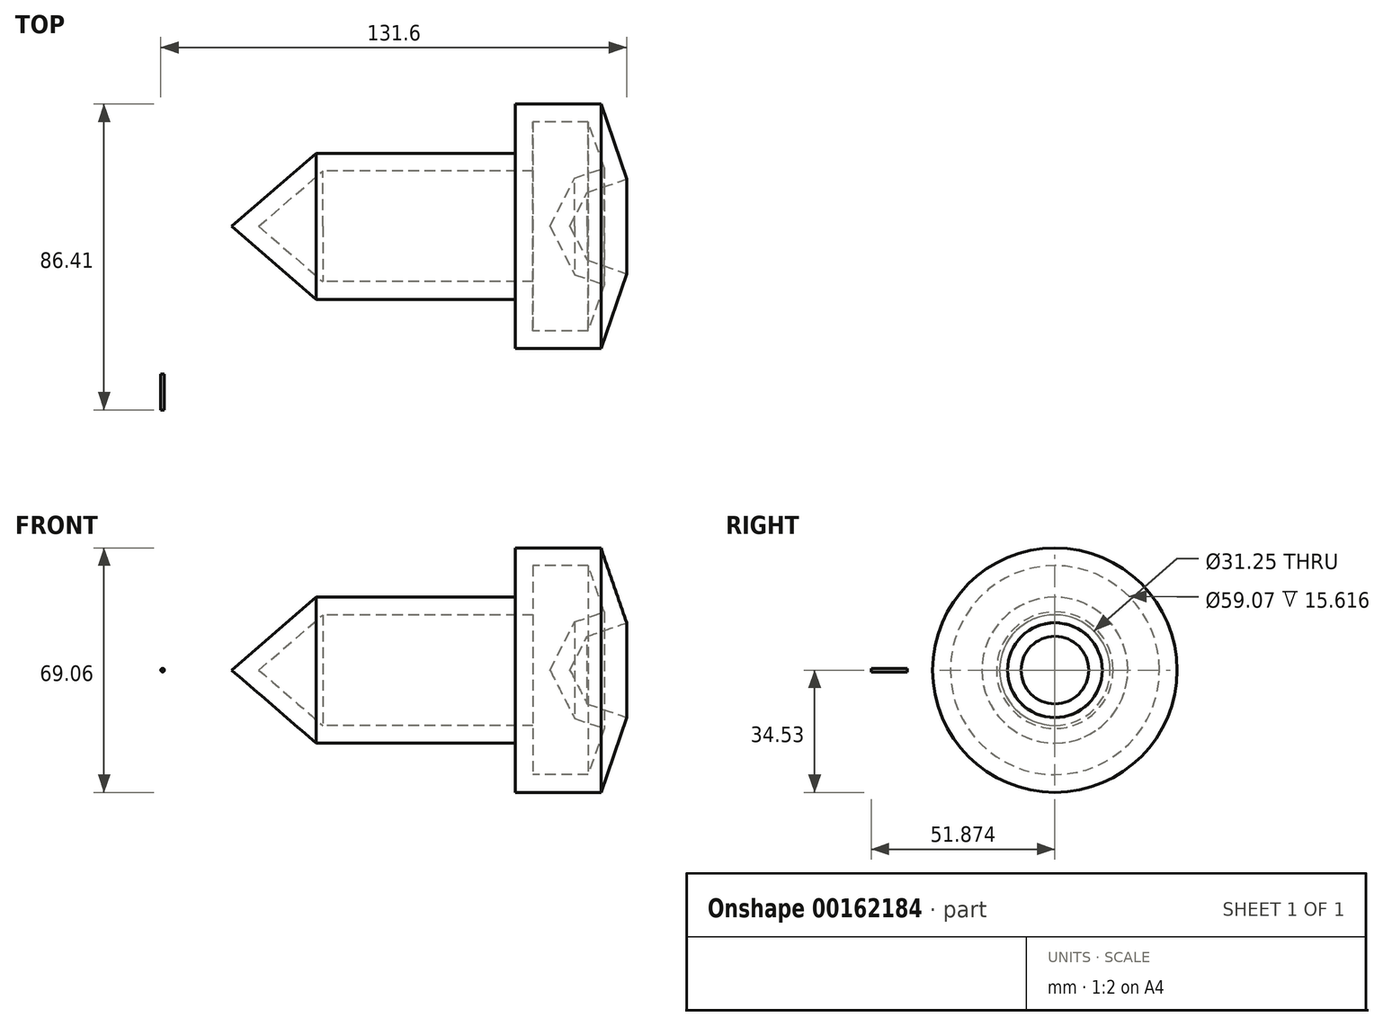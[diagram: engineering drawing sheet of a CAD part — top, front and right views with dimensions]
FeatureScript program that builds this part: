
annotation { "Feature Type Name" : "Feature", "Feature Type Description" : "" }
export const myFeature = defineFeature(function(context is Context, id is Id, definition is map)
    precondition{}
    {
        {
            var Q0;
            Q0=qCreatedBy(makeId("Top.planeOp"),FACE);
            var sketch = newSketch(context, id + "F0", { "sketchPlane" : qUnion([Q0])});
            skLineSegment(sketch, "E0", {"start": v(27.18, 41.72) * mm, "end": v(115.07, 41.72) * mm, "construction": true});
            skLineSegment(sketch, "E1", {"start": v(19.53, 41.72) * mm, "end": v(43.41, 62.35) * mm});
            skLineSegment(sketch, "E2", {"start": v(43.41, 62.35) * mm, "end": v(99.65, 62.35) * mm});
            skLineSegment(sketch, "E3", {"start": v(99.65, 62.35) * mm, "end": v(99.65, 76.26) * mm});
            skLineSegment(sketch, "E4", {"start": v(99.65, 76.26) * mm, "end": v(123.84, 76.26) * mm});
            skLineSegment(sketch, "E5", {"start": v(123.84, 76.26) * mm, "end": v(131.1, 55.1) * mm});
            skLineSegment(sketch, "E6", {"start": v(131.1, 55.1) * mm, "end": v(119.96, 51.27) * mm});
            skLineSegment(sketch, "E7", {"start": v(119.96, 51.27) * mm, "end": v(115.07, 41.72) * mm});
            skLineSegment(sketch, "E8.0", {"start": v(116.43, 55.35) * mm, "end": v(109.45, 41.72) * mm});
            skLineSegment(sketch, "E8.1", {"start": v(124.74, 58.2) * mm, "end": v(116.43, 55.35) * mm});
            skLineSegment(sketch, "E8.2", {"start": v(120.27, 71.26) * mm, "end": v(124.74, 58.2) * mm});
            skLineSegment(sketch, "E8.3", {"start": v(27.18, 41.72) * mm, "end": v(45.27, 57.35) * mm});
            skLineSegment(sketch, "E8.4", {"start": v(45.27, 57.35) * mm, "end": v(104.65, 57.35) * mm});
            skLineSegment(sketch, "E8.5", {"start": v(104.65, 57.35) * mm, "end": v(104.65, 71.26) * mm});
            skLineSegment(sketch, "E8.6", {"start": v(104.65, 71.26) * mm, "end": v(120.27, 71.26) * mm});
            skLineSegment(sketch, "E9", {"start": v(19.53, 41.72) * mm, "end": v(27.18, 41.72) * mm});
            skLineSegment(sketch, "E10", {"start": v(115.07, 41.72) * mm, "end": v(109.45, 41.72) * mm});
            skSolve(sketch);
        }
        {
            var Q0;
            Q0=makeQuery(id+"F0.imprint","IMPRINT",FACE,{"disambiguationData":[TD([[makeQuery(id+"F0.imprint","IMPRINT",EDGE,{"derivedFrom":sQuery(id+"F0.wireOp",EDGE,"E1")}),-1.0]])]});
            var Q1;
            Q1=sQuery(id+"F0.wireOp",EDGE,"E0");
            revolve(context, id + "F1", {"entities" : qUnion([Q0]), "axis" : qUnion([Q1]), "revolveType" : RevolveType.FULL});
        }
        {
            var Q0;
            Q0=qCreatedBy(makeId("Front.planeOp"),FACE);
            var sketch = newSketch(context, id + "F2", { "sketchPlane" : qUnion([Q0])});
            skCircle(sketch, "E11", {"center": v(0, 0) * mm, "radius": 0.5 * mm});
            skCircle(sketch, "E12", {"center": v(0, 0) * mm, "radius": 0.77 * mm});
            skSolve(sketch);
        }
        {
            var Q0;
            Q0=makeQuery(id+"F2.imprint","IMPRINT",FACE,{"disambiguationData":[TD([[makeQuery(id+"F2.imprint","IMPRINT",EDGE,{"derivedFrom":sQuery(id+"F2.wireOp",EDGE,"E11")}),1.0]])]});
            extrude(context, id + "F3", {"entities" : qUnion([Q0]), "depth" : 10.15 * mm});
        }
    });
